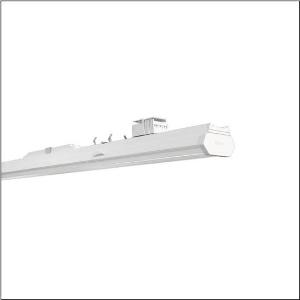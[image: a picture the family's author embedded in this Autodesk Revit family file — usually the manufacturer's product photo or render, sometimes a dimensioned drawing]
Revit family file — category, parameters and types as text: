
# Revit family: licross_r__11_protected_ho_51tp13cn4e5s_b79e
name_source: partatom
category: Lighting Fixtures
units: mm (PartAtom-declared; Revit-internal decimal feet)

## family parameters
Cut with Voids When Loaded = No
Host = Face
Light Source = No
Part Type = Normal
Room Calculation Point = No
Round Connector Dimension = Use Diameter
Shared = No

## types (1)
- --- (1 x LED, 14500 lm, 77.6 W, 4000K)
    Apparent Load = 78 VA
    CIE Flux Codes = 89 96 99 100 99
    Color Rendering = 80
    Color Temperature = 4000K
    Default Elevation = 1800 mm
    Description = Licross® 11 Protected HO, luminaire insert, of sheet steel, galvanised, coil coated, white, length: 1.500mm, width: 90mm, height: 101mm, LED rated luminous flux: 14.500lm, light colour: 840, control gear: ON/OFF Multilumen, CLOi, with plug, 3-pole, with phase selection, mains connection: 220..240V, AC, 50/60Hz, start of lifetime: 78W, end of service life: 87W, halogen-free wiring, primary light control with lens, of plastic, primary optical cover: cover, of PMMA, light emission: direct distribution, primary light characteristic: symmetric, protection rating (complete): IP64, insulation class (complete): insulation class I (protective earthing), certification: CE, ENEC, VDE, UKCA, protection symbol: D if used in an environment with conductive dust loads with corresponding accessories, impact resistance: IK06, permissible ambient temperature for indoor applications: -35..+35°C, corresponds to IFS (International Featured Standards) requirements for safety and quality in the food industry, reducing of maximum allowable ambient temperature of 5°C with ceiling mounting, LABS conformity tested according to VDMA 24364:2018-05, packaging unit: 1 piece
    Height = 92 mm
    Lamp = 1 x LED
    Lamp Light Flux = 14500 lm
    Lamp Power = 77.6 W
    Lamp count = 1
    Length = 1500 mm
    Luminous efficacy = 187 lm/W
    Manufacturer = Siteco
    ModVariant = No
    Model = 51TP13CN4E5S
    Mounting Place = Ceiling
    Mounting Type = Pendant
    Number of Poles = 1
    OnlyDefault = Yes
    Power Factor = 1
    Product Name = Licross® 11 Protected HO
    Product group = luminaire insert
    ProductGroupID = 901
    Protection Class = Protection class I
    Protection Degree = IP 64
    RLX_Detail_Level = 1
    RLX_Emergency_Light_Flux = 0 lm
    RLX_Emergency_Type = 0
    RLX_Emergency_Type_DB = No
    RlxData = <blob elided: 22025 chars, md5=38faaed8>
    Socket = socket
    Standby Power = 0 W
    System Light Flux = 14500 lm
    System Power = 78 W
    Type Comments = factory setting: luminous flux: 100 % | (A | C | E) | 181 mA
    Type Image = l_1256148.jpg
    URL = http://relux.com
    VarID = @adj_019199
    Voltage = 0 V
    Weight = 0.00 kg
    Width = 88 mm

## geometry (parser evidence)
native form markers: Blend x4, Sweep x12
no freeform markers — native parametric forms only
